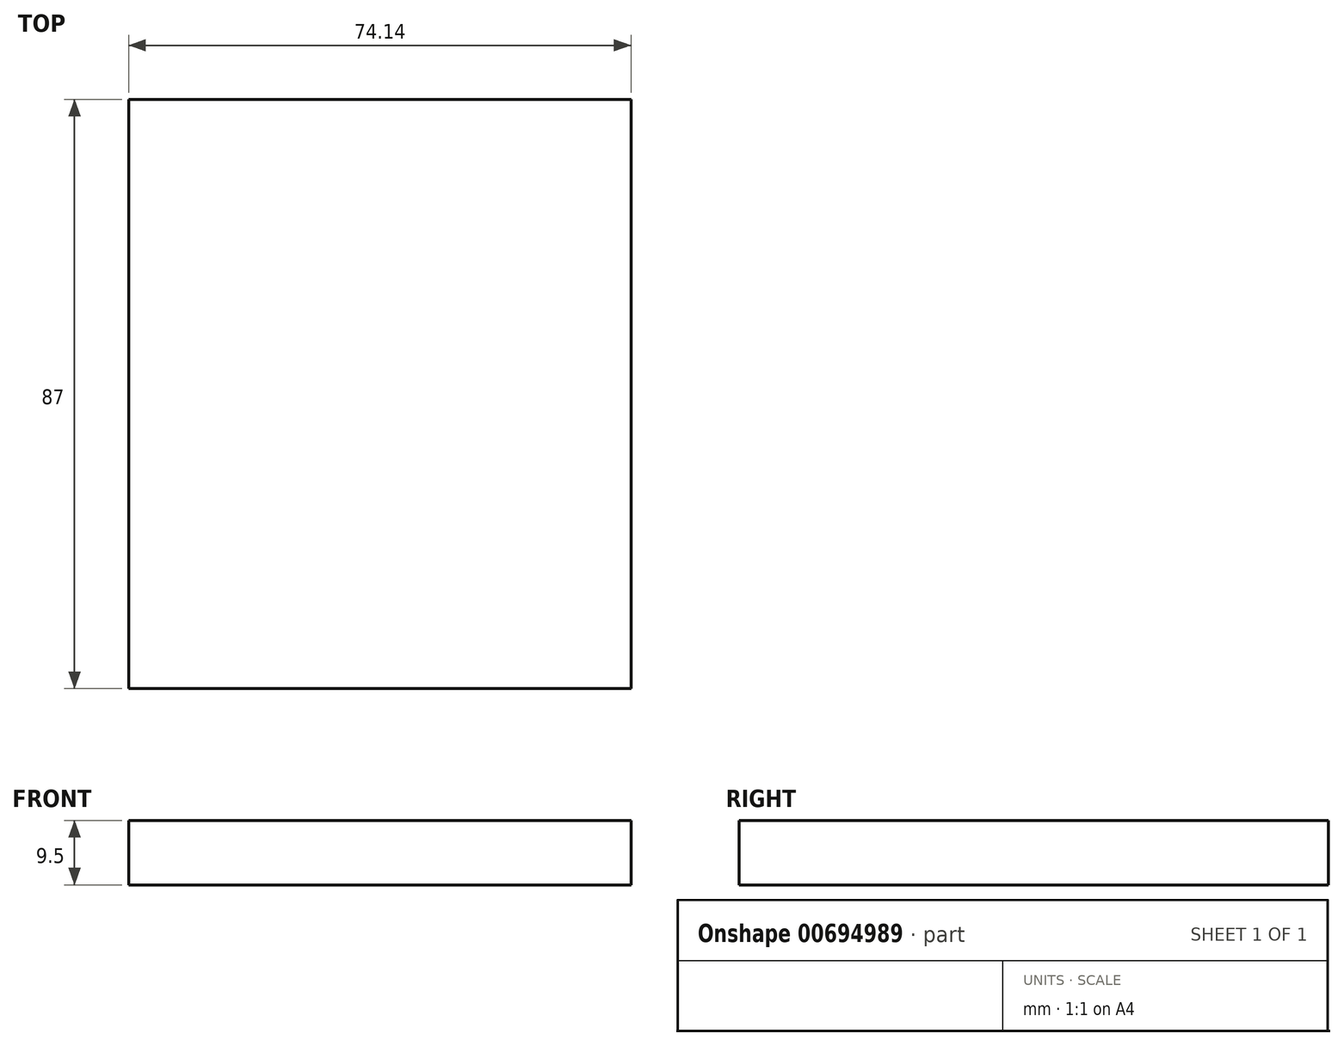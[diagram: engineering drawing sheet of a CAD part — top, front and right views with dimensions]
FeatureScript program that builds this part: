
annotation { "Feature Type Name" : "Feature", "Feature Type Description" : "" }
export const myFeature = defineFeature(function(context is Context, id is Id, definition is map)
    precondition{}
    {
        {
            var Q0;
            Q0=qCreatedBy(makeId("Top.planeOp"),FACE);
            var sketch = newSketch(context, id + "F0", { "sketchPlane" : qUnion([Q0])});
            skLineSegment(sketch, "E0.bottom", {"start": v(-38.37, 40) * mm, "end": v(35.77, 40) * mm});
            skLineSegment(sketch, "E0.top", {"start": v(-38.37, -47) * mm, "end": v(35.77, -47) * mm});
            skLineSegment(sketch, "E0.left", {"start": v(-38.37, 40) * mm, "end": v(-38.37, -47) * mm});
            skLineSegment(sketch, "E0.right", {"start": v(35.77, 40) * mm, "end": v(35.77, -47) * mm});
            skSolve(sketch);
        }
        {
            var Q0;
            Q0=makeQuery(id+"F0.imprint","IMPRINT",FACE,{"disambiguationData":[TD([[makeQuery(id+"F0.imprint","IMPRINT",EDGE,{"derivedFrom":sQuery(id+"F0.wireOp",EDGE,"E0.bottom")}),-1.0]])]});
            extrude(context, id + "F1", {"entities" : qUnion([Q0]), "depth" : 9.5 * mm, "offsetDistance" : 25 * mm});
        }
    });
